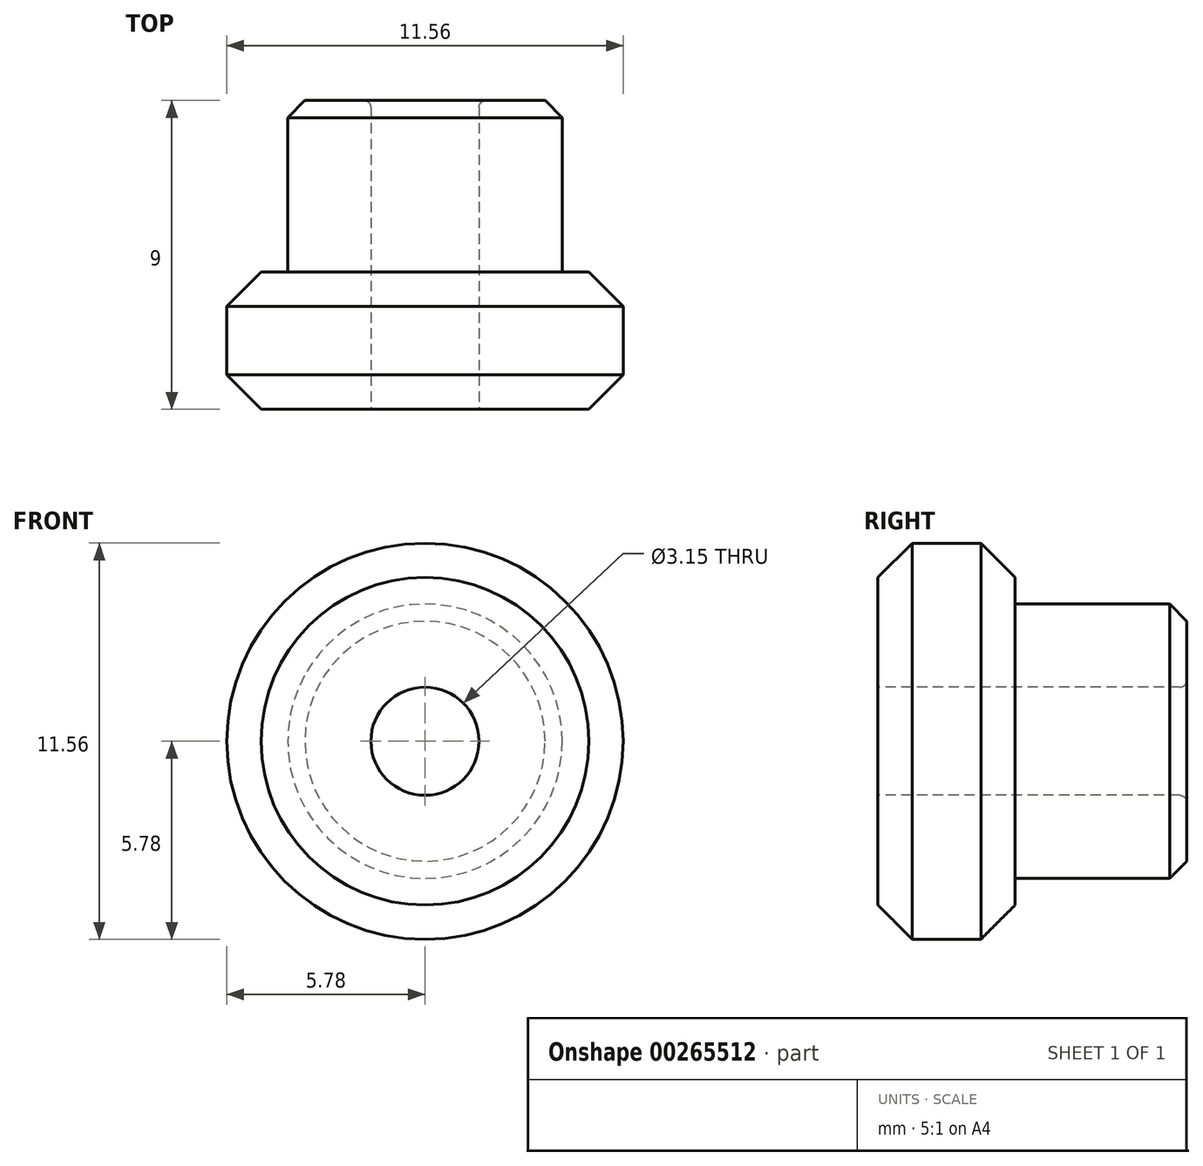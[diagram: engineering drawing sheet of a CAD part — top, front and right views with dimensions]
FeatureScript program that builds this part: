
annotation { "Feature Type Name" : "Feature", "Feature Type Description" : "" }
export const myFeature = defineFeature(function(context is Context, id is Id, definition is map)
    precondition{}
    {
        {
            var Q0;
            Q0=qCreatedBy(makeId("Front.planeOp"),FACE);
            var sketch = newSketch(context, id + "F0", { "sketchPlane" : qUnion([Q0])});
            skCircle(sketch, "E0", {"center": v(0, 0) * mm, "radius": 4 * mm});
            skSolve(sketch);
        }
        {
            var Q0;
            Q0=makeQuery(id+"F0.imprint","IMPRINT",FACE,{"disambiguationData":[TD([[makeQuery(id+"F0.imprint","IMPRINT",EDGE,{"derivedFrom":sQuery(id+"F0.wireOp",EDGE,"E0")}),1.0]])]});
            extrude(context, id + "F1", {"entities" : qUnion([Q0]), "depth" : 5 * mm});
        }
        {
            var Q0;
            Q0=makeQuery(id+"F1.opExtrude","CAP_FACE",FACE,{"disambiguationData":[OSD([sQuery(id+"F0.wireOp",EDGE,"E0")])],"isStart":false});
            var sketch = newSketch(context, id + "F2", { "sketchPlane" : qUnion([Q0])});
            skCircle(sketch, "E1", {"center": v(0, 0) * mm, "radius": 5.78 * mm});
            skSolve(sketch);
        }
        {
            var Q0;
            Q0=makeQuery(id+"F2.imprint","IMPRINT",FACE,{"disambiguationData":[TD([[makeQuery(id+"F2.imprint","IMPRINT",EDGE,{"derivedFrom":sQuery(id+"F2.wireOp",EDGE,"E1")}),1.0]])]});
            var Q1;
            Q1=makeQuery(id+"F2.imprint","IMPRINT",FACE,{"disambiguationData":[TD([[makeQuery(id+"F2.imprint","IMPRINT",EDGE,{"derivedFrom":makeQuery(id+"F1.opExtrude","CAP_EDGE",EDGE,{"disambiguationData":[OSD([sQuery(id+"F0.wireOp",EDGE,"E0")])],"isStart":false})}),1.0]])]});
            extrude(context, id + "F3", {"entities" : qUnion([Q0, Q1]), "operationType" : NewBodyOperationType.ADD, "depth" : 4 * mm});
        }
        {
            var Q0;
            Q0=makeQuery(id+"F3.opExtrude","CAP_FACE",FACE,{"disambiguationData":[OSD([sQuery(id+"F2.wireOp",EDGE,"E1")])],"isStart":false});
            var sketch = newSketch(context, id + "F4", { "sketchPlane" : qUnion([Q0])});
            skCircle(sketch, "E2", {"center": v(0, 0) * mm, "radius": 1.57 * mm});
            skSolve(sketch);
        }
        {
            var Q0;
            Q0=makeQuery(id+"F4.imprint","IMPRINT",FACE,{"disambiguationData":[TD([[makeQuery(id+"F4.imprint","IMPRINT",EDGE,{"derivedFrom":sQuery(id+"F4.wireOp",EDGE,"E2")}),1.0]])]});
            extrude(context, id + "F5", {"entities" : qUnion([Q0]), "operationType" : NewBodyOperationType.REMOVE, "oppositeDirection" : true, "depth" : 10 * mm});
        }
        {
            var Q0;
            Q0=makeQuery(id+"F3.opExtrude","CAP_EDGE",EDGE,{"disambiguationData":[OSD([sQuery(id+"F2.wireOp",EDGE,"E1")])],"isStart":false});
            var Q1;
            Q1=makeQuery(id+"F3.opExtrude","CAP_EDGE",EDGE,{"disambiguationData":[OSD([sQuery(id+"F2.wireOp",EDGE,"E1")])],"isStart":true});
            chamfer(context, id + "F6", {"entities" : qUnion([Q0, Q1]), "width" : 1 * mm, "tangentPropagation" : true});
        }
        {
            var Q0;
            Q0=makeQuery(id+"F1.opExtrude","CAP_EDGE",EDGE,{"disambiguationData":[OSD([sQuery(id+"F0.wireOp",EDGE,"E0")])],"isStart":true});
            chamfer(context, id + "F7", {"entities" : qUnion([Q0]), "width" : 0.5 * mm, "tangentPropagation" : true});
        }
        {
            var Q0;
            Q0=makeQuery(id+"F5.boolean.opBoolean","COPY",EDGE,{"derivedFrom":makeQuery(id+"F5.opExtrude","CAP_EDGE",EDGE,{"disambiguationData":[OSD([sQuery(id+"F4.wireOp",EDGE,"E2")])],"isStart":true})});
            var Q1;
            Q1=makeQuery(id+"F5.boolean.opBoolean","INTERSECT",EDGE,{"derivedFrom":[makeQuery(id+"F1.opExtrude","CAP_FACE",FACE,{"disambiguationData":[OSD([sQuery(id+"F0.wireOp",EDGE,"E0")])],"isStart":true}),makeQuery(id+"F5.opExtrude","SWEPT_FACE",FACE,{"disambiguationData":[OSD([sQuery(id+"F4.wireOp",EDGE,"E2")])]})]});
            fillet(context, id + "F8", {"entities" : qUnion([Q0, Q1]), "radius" : 0.2 * mm, "tangentPropagation" : true, "allowEdgeOverflow" : false});
        }
    });
